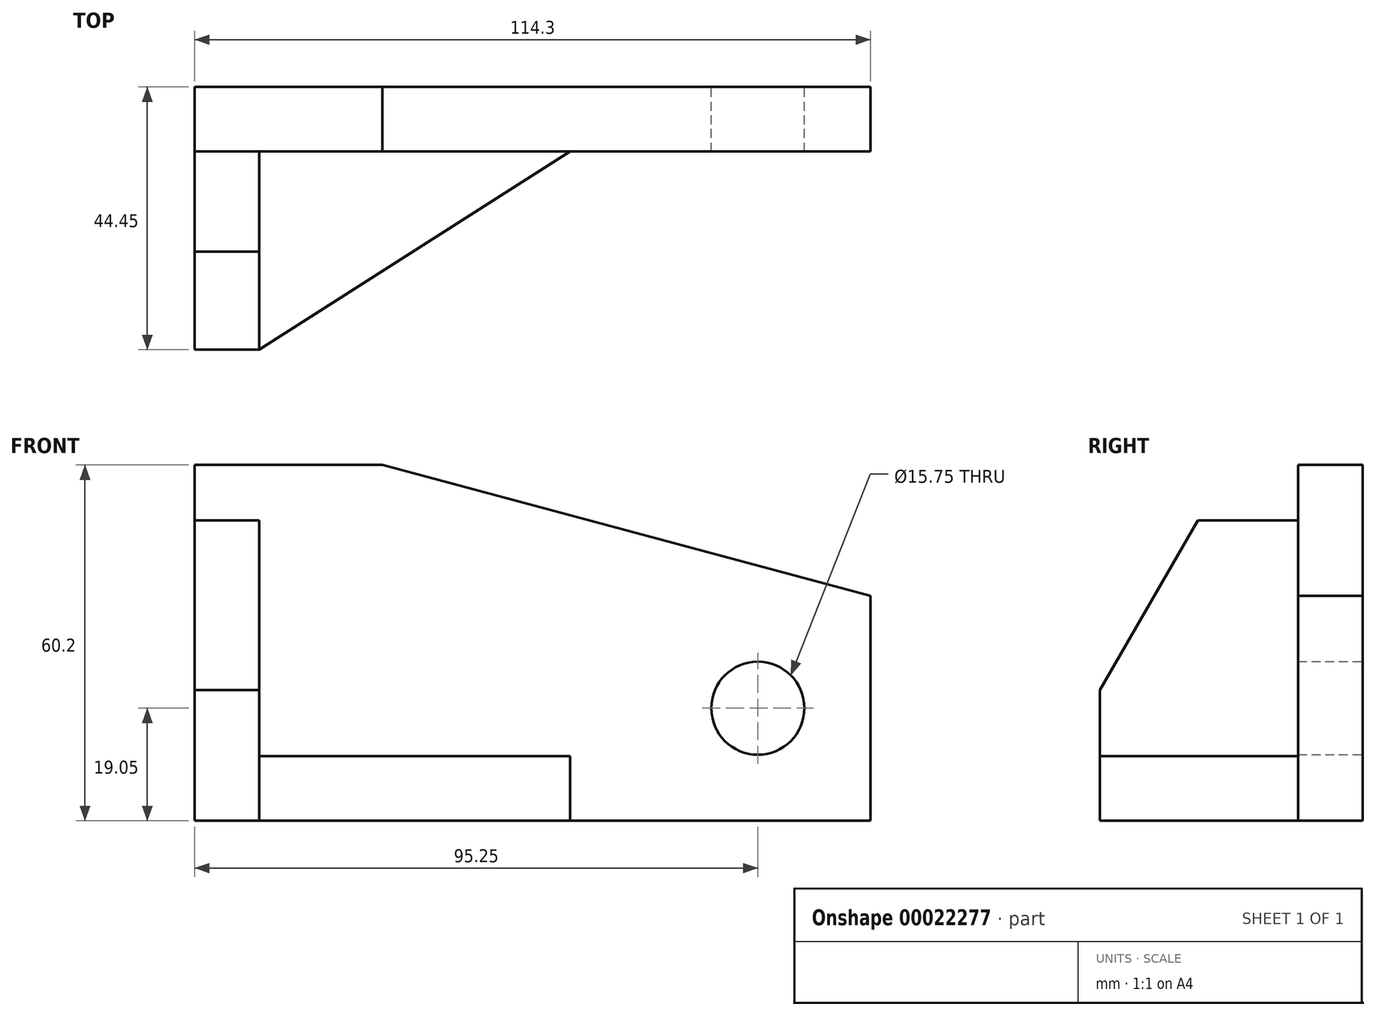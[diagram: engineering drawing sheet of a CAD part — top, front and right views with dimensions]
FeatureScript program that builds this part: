
annotation { "Feature Type Name" : "Feature", "Feature Type Description" : "" }
export const myFeature = defineFeature(function(context is Context, id is Id, definition is map)
    precondition{}
    {
        {
            var Q0;
            Q0=qCreatedBy(makeId("Front.planeOp"),FACE);
            var sketch = newSketch(context, id + "F0", { "sketchPlane" : qUnion([Q0])});
            skLineSegment(sketch, "E0.bottom", {"start": v(0, 0) * mm, "end": v(-114.3, 0) * mm});
            skLineSegment(sketch, "E0.top", {"start": v(-82.55, 60.2) * mm, "end": v(-114.3, 60.2) * mm});
            skLineSegment(sketch, "E0.left", {"start": v(0, 0) * mm, "end": v(0, 38.08) * mm});
            skLineSegment(sketch, "E0.right", {"start": v(-114.3, 0) * mm, "end": v(-114.3, 60.2) * mm});
            skLineSegment(sketch, "E1", {"start": v(-82.55, 60.2) * mm, "end": v(0, 38.08) * mm});
            skCircle(sketch, "E2", {"center": v(-19.05, 19.05) * mm, "radius": 7.87 * mm});
            skSolve(sketch);
        }
        {
            var Q0;
            Q0=makeQuery(id+"F0.imprint","IMPRINT",FACE,{"disambiguationData":[TD([[makeQuery(id+"F0.imprint","IMPRINT",EDGE,{"derivedFrom":sQuery(id+"F0.wireOp",EDGE,"E0.bottom")}),-1.0]])]});
            extrude(context, id + "F1", {"entities" : qUnion([Q0]), "depth" : 10.92 * mm});
        }
        {
            var Q0;
            Q0=makeQuery(id+"F1.opExtrude","SWEPT_FACE",FACE,{"disambiguationData":[OSD([sQuery(id+"F0.wireOp",EDGE,"E0.right")])]});
            var sketch = newSketch(context, id + "F2", { "sketchPlane" : qUnion([Q0])});
            skLineSegment(sketch, "E3.bottom", {"start": v(10.92, 0) * mm, "end": v(44.45, 0) * mm});
            skLineSegment(sketch, "E3.top", {"start": v(10.92, 50.8) * mm, "end": v(27.88, 50.8) * mm});
            skLineSegment(sketch, "E3.left", {"start": v(10.92, 0) * mm, "end": v(10.92, 50.8) * mm});
            skLineSegment(sketch, "E3.right", {"start": v(44.45, 0) * mm, "end": v(44.45, 22.1) * mm});
            skLineSegment(sketch, "E4", {"start": v(27.88, 50.8) * mm, "end": v(44.45, 22.1) * mm});
            skSolve(sketch);
        }
        {
            var Q0;
            Q0=makeQuery(id+"F2.imprint","IMPRINT",FACE,{"disambiguationData":[TD([[makeQuery(id+"F2.imprint","IMPRINT",EDGE,{"derivedFrom":sQuery(id+"F2.wireOp",EDGE,"E3.bottom")}),1.0]])]});
            extrude(context, id + "F3", {"entities" : qUnion([Q0]), "oppositeDirection" : true, "depth" : 10.92 * mm});
        }
        {
            var Q0;
            Q0=makeQuery(id+"F3.opExtrude","SWEPT_FACE",FACE,{"disambiguationData":[OSD([sQuery(id+"F2.wireOp",EDGE,"E3.bottom")])]});
            var sketch = newSketch(context, id + "F4", { "sketchPlane" : qUnion([Q0])});
            skLineSegment(sketch, "E5.bottom", {"start": v(-103.38, 10.92) * mm, "end": v(-50.8, 10.92) * mm});
            skLineSegment(sketch, "E5.left", {"start": v(-103.38, 10.92) * mm, "end": v(-103.38, 44.45) * mm});
            skLineSegment(sketch, "E6", {"start": v(-103.38, 44.45) * mm, "end": v(-50.8, 10.92) * mm});
            skSolve(sketch);
        }
        {
            var Q0;
            Q0=makeQuery(id+"F4.imprint","IMPRINT",FACE,{"disambiguationData":[TD([[makeQuery(id+"F4.imprint","IMPRINT",EDGE,{"derivedFrom":sQuery(id+"F4.wireOp",EDGE,"E5.bottom")}),1.0]])]});
            extrude(context, id + "F5", {"entities" : qUnion([Q0]), "oppositeDirection" : true, "depth" : 10.92 * mm});
        }
    });
